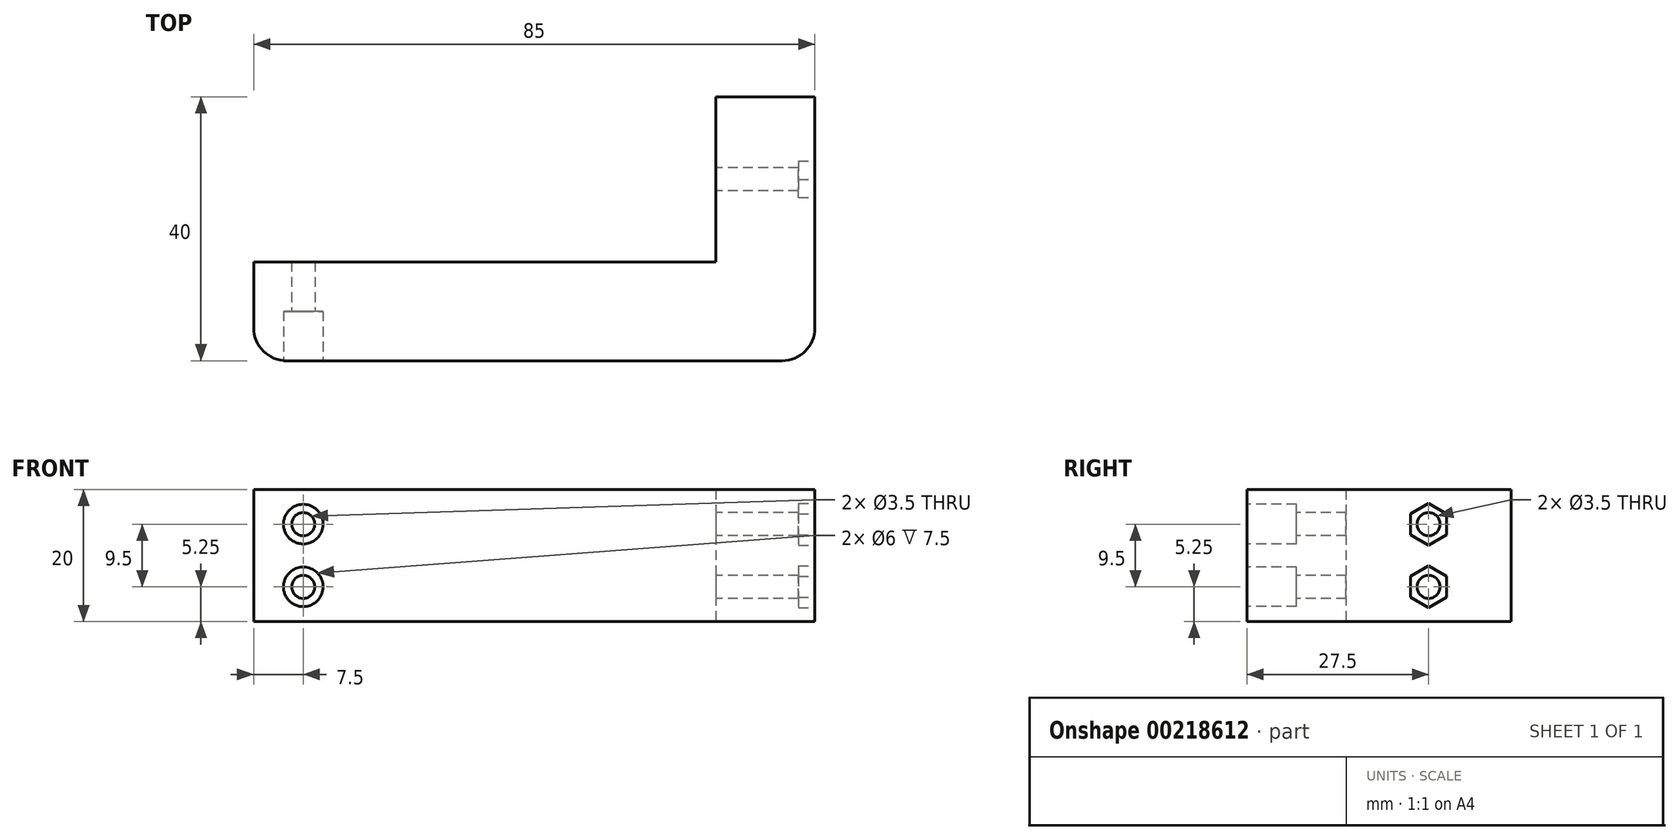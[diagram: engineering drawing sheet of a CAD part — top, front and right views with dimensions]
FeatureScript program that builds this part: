
annotation { "Feature Type Name" : "Feature", "Feature Type Description" : "" }
export const myFeature = defineFeature(function(context is Context, id is Id, definition is map)
    precondition{}
    {
        {
            var Q0;
            Q0=qCreatedBy(makeId("Top.planeOp"),FACE);
            var sketch = newSketch(context, id + "F0", { "sketchPlane" : qUnion([Q0])});
            skLineSegment(sketch, "E0", {"start": v(0, 0) * mm, "end": v(85, 0) * mm});
            skLineSegment(sketch, "E1", {"start": v(85, 0) * mm, "end": v(85, 40) * mm});
            skLineSegment(sketch, "E2", {"start": v(85, 40) * mm, "end": v(70, 40) * mm});
            skLineSegment(sketch, "E3", {"start": v(70, 40) * mm, "end": v(70, 15) * mm});
            skLineSegment(sketch, "E4", {"start": v(70, 15) * mm, "end": v(0, 15) * mm});
            skLineSegment(sketch, "E5", {"start": v(0, 15) * mm, "end": v(0, 0) * mm});
            skSolve(sketch);
        }
        {
            var Q0;
            Q0 = qSketchRegion(id + "F0", true);
            extrude(context, id + "F1", {"entities" : qUnion([Q0]), "depth" : 20 * mm, "offsetDistance" : 25 * mm});
        }
        {
            var Q0;
            Q0=makeQuery(id+"F1.opExtrude","SWEPT_FACE",FACE,{"disambiguationData":[OSD([sQuery(id+"F0.wireOp",EDGE,"E0")])]});
            var sketch = newSketch(context, id + "F2", { "sketchPlane" : qUnion([Q0])});
            skLineSegment(sketch, "E6", {"start": v(0, 10) * mm, "end": v(15, 10) * mm, "construction": true});
            skCircle(sketch, "E7", {"center": v(7.5, 14.75) * mm, "radius": 1.75 * mm});
            skPoint(sketch, "E8", {"position": v(7.5, 10) * mm});
            skCircle(sketch, "E9.MirrorC", {"center": v(7.5, 5.25) * mm, "radius": 1.75 * mm});
            skSolve(sketch);
        }
        {
            var Q0;
            Q0 = qSketchRegion(id + "F2", true);
            extrude(context, id + "F3", {"entities" : qUnion([Q0]), "operationType" : NewBodyOperationType.REMOVE, "endBound" : BoundingType.THROUGH_ALL, "oppositeDirection" : true, "depth" : 25 * mm, "offsetDistance" : 25 * mm});
        }
        {
            var Q0;
            Q0=makeQuery(id+"F1.opExtrude","SWEPT_FACE",FACE,{"disambiguationData":[OSD([sQuery(id+"F0.wireOp",EDGE,"E0")])]});
            var sketch = newSketch(context, id + "F4", { "sketchPlane" : qUnion([Q0])});
            skCircle(sketch, "E10", {"center": v(7.5, 14.75) * mm, "radius": 3 * mm});
            skCircle(sketch, "E11", {"center": v(7.5, 5.25) * mm, "radius": 3 * mm});
            skSolve(sketch);
        }
        {
            var Q0;
            Q0 = qSketchRegion(id + "F4", true);
            extrude(context, id + "F5", {"entities" : qUnion([Q0]), "operationType" : NewBodyOperationType.REMOVE, "oppositeDirection" : true, "depth" : 7.5 * mm, "offsetDistance" : 25 * mm});
        }
        {
            var Q0;
            Q0=makeQuery(id+"F1.opExtrude","SWEPT_FACE",FACE,{"disambiguationData":[OSD([sQuery(id+"F0.wireOp",EDGE,"E3")])]});
            var sketch = newSketch(context, id + "F6", { "sketchPlane" : qUnion([Q0])});
            skLineSegment(sketch, "E12", {"start": v(-40, 10) * mm, "end": v(-15, 10) * mm, "construction": true});
            skCircle(sketch, "E13", {"center": v(-27.5, 14.75) * mm, "radius": 1.75 * mm});
            skPoint(sketch, "E13.centerSnap0", {"position": v(-27.5, 10) * mm});
            skCircle(sketch, "E14.MirrorC", {"center": v(-27.5, 5.25) * mm, "radius": 1.75 * mm});
            skSolve(sketch);
        }
        {
            var Q0;
            Q0 = qSketchRegion(id + "F6", true);
            extrude(context, id + "F7", {"entities" : qUnion([Q0]), "operationType" : NewBodyOperationType.REMOVE, "endBound" : BoundingType.THROUGH_ALL, "oppositeDirection" : true, "depth" : 25 * mm, "offsetDistance" : 25 * mm});
        }
        {
            var Q0;
            Q0=makeQuery(id+"F1.opExtrude","SWEPT_EDGE",EDGE,{"disambiguationData":[OSD([sQuery(id+"F0.wireOp",EDGE,"E0"),sQuery(id+"F0.wireOp",EDGE,"E1")])]});
            var Q1;
            Q1=makeQuery(id+"F1.opExtrude","SWEPT_EDGE",EDGE,{"disambiguationData":[OSD([sQuery(id+"F0.wireOp",EDGE,"E0"),sQuery(id+"F0.wireOp",EDGE,"E5")])]});
            fillet(context, id + "F8", {"entities" : qUnion([Q0, Q1]), "tangentPropagation" : true, "radius" : 5 * mm, "defaultsChanged" : false, "vertexSettings" : [], "allowEdgeOverflow" : false});
        }
        {
            var Q0;
            Q0=makeQuery(id+"F1.opExtrude","SWEPT_FACE",FACE,{"disambiguationData":[OSD([sQuery(id+"F0.wireOp",EDGE,"E1")])]});
            var sketch = newSketch(context, id + "F9", { "sketchPlane" : qUnion([Q0])});
            skCircle(sketch, "E15.cCircle", {"center": v(27.5, 14.75) * mm, "radius": 2.75 * mm, "construction": true});
            skLineSegment(sketch, "E15.0", {"start": v(30.25, 13.16) * mm, "end": v(27.5, 11.57) * mm});
            skLineSegment(sketch, "E15.1", {"start": v(27.5, 11.57) * mm, "end": v(24.75, 13.16) * mm});
            skLineSegment(sketch, "E15.2", {"start": v(24.75, 13.16) * mm, "end": v(24.75, 16.34) * mm});
            skLineSegment(sketch, "E15.3", {"start": v(24.75, 16.34) * mm, "end": v(27.5, 17.93) * mm});
            skLineSegment(sketch, "E15.4", {"start": v(27.5, 17.93) * mm, "end": v(30.25, 16.34) * mm});
            skLineSegment(sketch, "E15.5", {"start": v(30.25, 16.34) * mm, "end": v(30.25, 13.16) * mm});
            skPoint(sketch, "E15.0.midPoint", {"position": v(28.88, 12.37) * mm});
            skLineSegment(sketch, "E16", {"start": v(40, 10) * mm, "end": v(18.68, 10) * mm, "construction": true});
            skLineSegment(sketch, "E17.MirrorCS", {"start": v(27.5, 8.43) * mm, "end": v(24.75, 6.84) * mm});
            skLineSegment(sketch, "E18.MirrorCS", {"start": v(27.5, 2.07) * mm, "end": v(30.25, 3.66) * mm});
            skLineSegment(sketch, "E19.MirrorCS", {"start": v(30.25, 6.84) * mm, "end": v(27.5, 8.43) * mm});
            skLineSegment(sketch, "E20.MirrorCS", {"start": v(24.75, 6.84) * mm, "end": v(24.75, 3.66) * mm});
            skPoint(sketch, "E21.MirrorP", {"position": v(28.88, 7.63) * mm});
            skLineSegment(sketch, "E22.MirrorCS", {"start": v(24.75, 3.66) * mm, "end": v(27.5, 2.07) * mm});
            skLineSegment(sketch, "E23.MirrorCS", {"start": v(30.25, 3.66) * mm, "end": v(30.25, 6.84) * mm});
            skCircle(sketch, "E24.MirrorC", {"center": v(27.5, 5.25) * mm, "radius": 2.75 * mm, "construction": true});
            skSolve(sketch);
        }
        {
            var Q0;
            Q0 = qSketchRegion(id + "F9", true);
            extrude(context, id + "F10", {"entities" : qUnion([Q0]), "operationType" : NewBodyOperationType.REMOVE, "oppositeDirection" : true, "depth" : 2.5 * mm, "offsetDistance" : 25 * mm});
        }
    });
